# Revit family: QF_BOURGEAT_Transtherm_Four_sur_pietement_haut_5GN1_1_et_7GN1_1
name_source: partatom
category: Equipement spécialisé
revit_build: Autodesk Revit 2015 (Build: 20140606_1530(x64)
units: mm (PartAtom-declared; Revit-internal decimal feet)

## types (4) — shared parameters
Certification = NF alimentaire
Débit Eau Adoucie = 0.0 L/s
Fabricant = BOURGEAT
Fréquence = 50 Hz
Hauteur hors tout = 1680 mm  [stored 5.51181 ft]
Indice de protection = IP25
Longueur hors tout = 682 mm
Nature isolant = Laine_de_roche(60mm)
Phase = 3
Poids net à vide = 28.00 kg
Profondeur hors tout = 720 mm  [stored 2.3622 ft]
Remarques Plomberie = Débit=0.000083L/s
Spécification du Fabricant = TRANS'THERM
URL catalogue = http://www.bourgeat.fr

## per-type parameters (varying)
| type | Consommation énergétique | Intensité nominale | Modèle | Poids | Puissance électrique  | Tension |
| 892205 + 895205 | 2.84Kwh/h | 15 A | 892205 + 895205 | 48Kg | 3500 W | 230 V |
| 892205 + 897500 + 895205 | 2.84Kwh/h | 15 A | 892205 + 897500 +895205 | 48Kg | 3500 W | 230 V |
| 892207 + 895207 | 4Kwh/h | 17 A | 892207 + 895207 | 55Kg | 6800 W | 400 V |
| 892207 + 897500 + 895207 | 4Kwh/h | 17 A | 892207 + 897500 + 895207 | 55Kg | 6800 W | 400 V |

note: column(s) folded — value = type name in every type: Type_de_modele

note: [stored X ft] marks values corroborated as IEEE doubles in the binary element streams (Revit-internal decimal feet)
